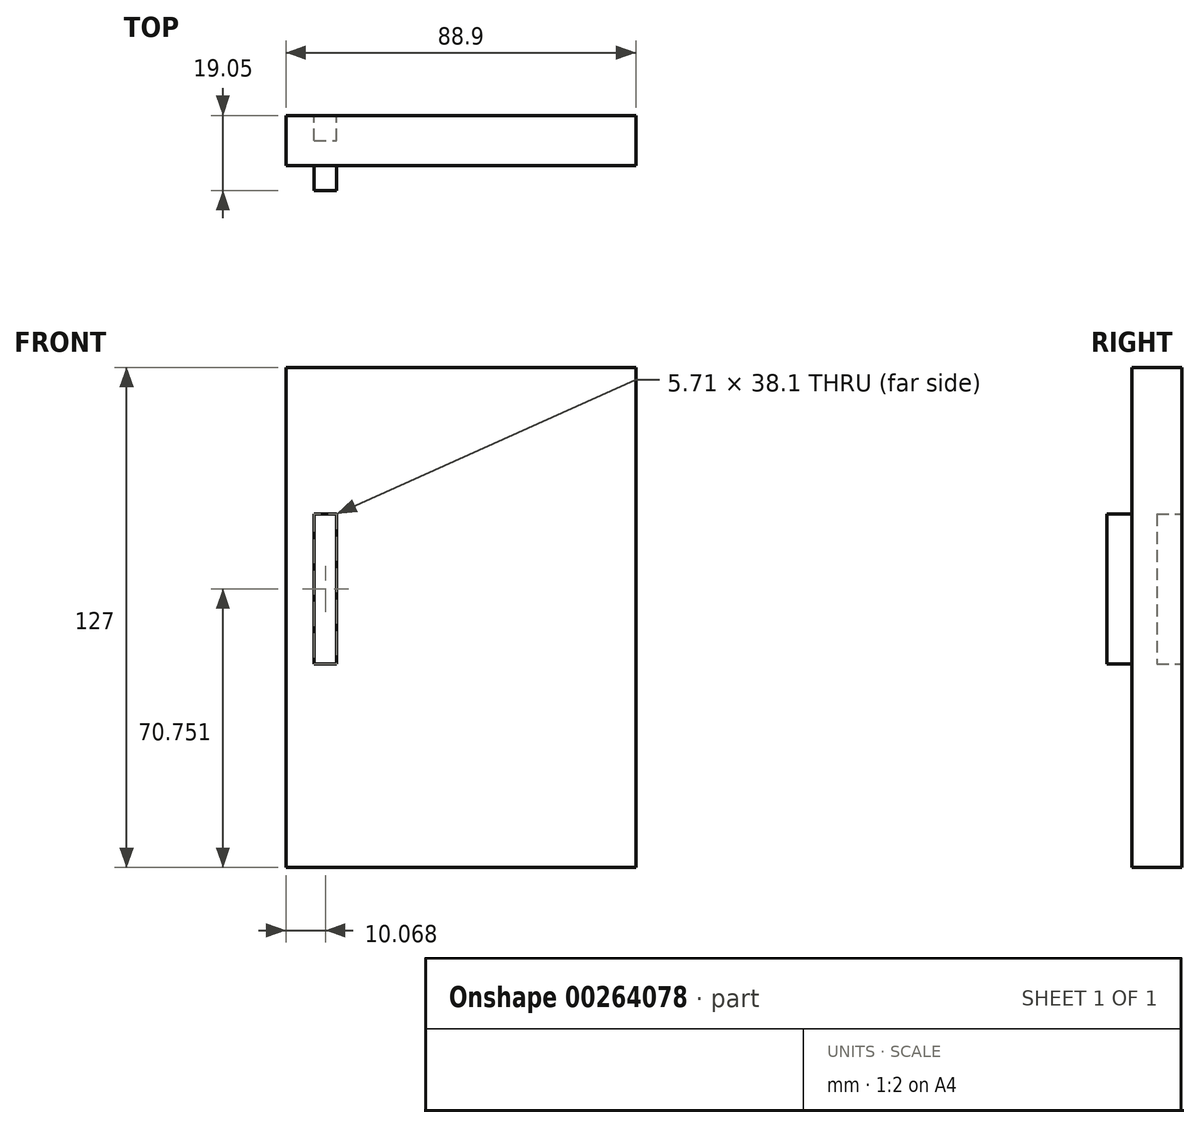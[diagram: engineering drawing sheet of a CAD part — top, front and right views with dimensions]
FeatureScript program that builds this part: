
annotation { "Feature Type Name" : "Feature", "Feature Type Description" : "" }
export const myFeature = defineFeature(function(context is Context, id is Id, definition is map)
    precondition{}
    {
        {
            var Q0;
            Q0=qCreatedBy(makeId("Front.planeOp"),FACE);
            var sketch = newSketch(context, id + "F0", { "sketchPlane" : qUnion([Q0])});
            skLineSegment(sketch, "E0.bottom", {"start": v(44.45, 63.5) * mm, "end": v(-44.45, 63.5) * mm});
            skLineSegment(sketch, "E0.top", {"start": v(44.45, -63.5) * mm, "end": v(-44.45, -63.5) * mm});
            skLineSegment(sketch, "E0.left", {"start": v(44.45, 63.5) * mm, "end": v(44.45, -63.5) * mm});
            skLineSegment(sketch, "E0.right", {"start": v(-44.45, 63.5) * mm, "end": v(-44.45, -63.5) * mm});
            skPoint(sketch, "E0.middle", {"position": v(0, 0) * mm});
            skLineSegment(sketch, "E1.bottom", {"start": v(-37.24, 26.3) * mm, "end": v(-31.52, 26.3) * mm});
            skLineSegment(sketch, "E1.top", {"start": v(-37.24, -11.8) * mm, "end": v(-31.52, -11.8) * mm});
            skLineSegment(sketch, "E1.left", {"start": v(-37.24, 26.3) * mm, "end": v(-37.24, -11.8) * mm});
            skLineSegment(sketch, "E1.right", {"start": v(-31.52, 26.3) * mm, "end": v(-31.52, -11.8) * mm});
            skSolve(sketch);
        }
        {
            var Q0;
            Q0=makeQuery(id+"F0.imprint","IMPRINT",FACE,{"disambiguationData":[TD([[makeQuery(id+"F0.imprint","IMPRINT",EDGE,{"derivedFrom":sQuery(id+"F0.wireOp",EDGE,"E0.bottom")}),1.0]])]});
            extrude(context, id + "F1", {"entities" : qUnion([Q0]), "endBound" : BoundingType.SYMMETRIC, "depth" : 12.7 * mm});
        }
        {
            var Q0;
            Q0=makeQuery(id+"F0.imprint","IMPRINT",FACE,{"disambiguationData":[TD([[makeQuery(id+"F0.imprint","IMPRINT",EDGE,{"derivedFrom":sQuery(id+"F0.wireOp",EDGE,"E1.bottom")}),-1.0]])]});
            extrude(context, id + "F2", {"entities" : qUnion([Q0]), "operationType" : NewBodyOperationType.ADD, "depth" : 12.7 * mm});
        }
    });
